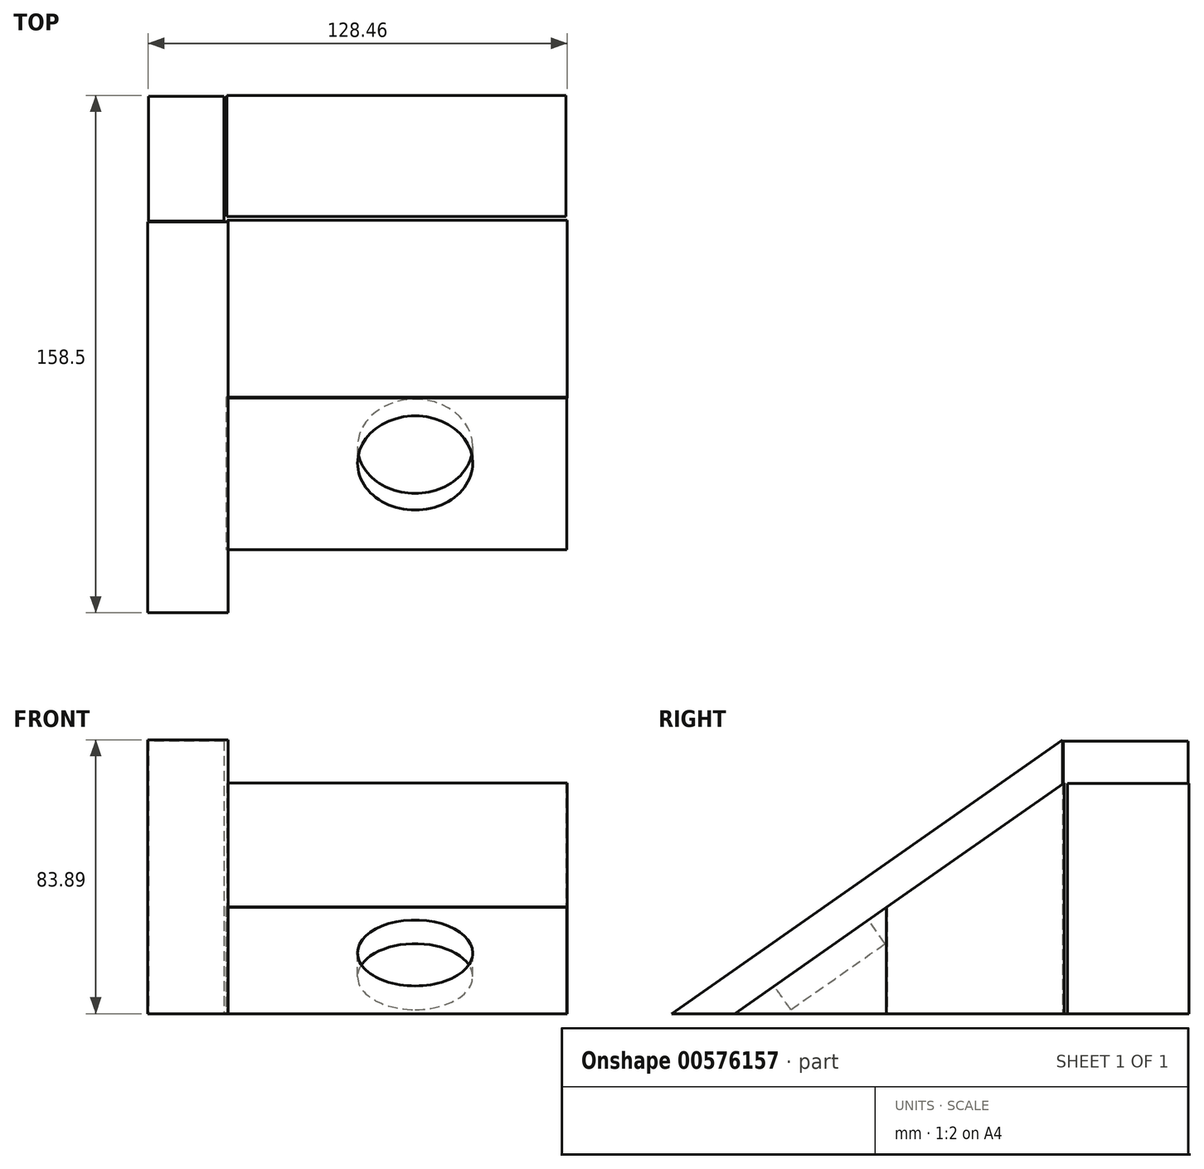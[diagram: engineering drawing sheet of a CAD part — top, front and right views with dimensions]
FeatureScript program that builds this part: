
annotation { "Feature Type Name" : "Feature", "Feature Type Description" : "" }
export const myFeature = defineFeature(function(context is Context, id is Id, definition is map)
    precondition{}
    {
        {
            var Q0;
            Q0=qCreatedBy(makeId("Top.planeOp"),FACE);
            var sketch = newSketch(context, id + "F0", { "sketchPlane" : qUnion([Q0])});
            skLineSegment(sketch, "E0.bottom", {"start": v(52.05, 27.2) * mm, "end": v(-52.05, 27.2) * mm});
            skLineSegment(sketch, "E0.top", {"start": v(52.05, -27.2) * mm, "end": v(-52.05, -27.2) * mm});
            skLineSegment(sketch, "E0.left", {"start": v(52.05, 27.2) * mm, "end": v(52.05, -27.2) * mm});
            skLineSegment(sketch, "E0.right", {"start": v(-52.05, 27.2) * mm, "end": v(-52.05, -27.2) * mm});
            skPoint(sketch, "E0.middle", {"position": v(0, 0) * mm});
            skSolve(sketch);
        }
        {
            var Q0;
            Q0=qCreatedBy(makeId("Top.planeOp"),FACE);
            var sketch = newSketch(context, id + "F1", { "sketchPlane" : qUnion([Q0])});
            skLineSegment(sketch, "E1.bottom", {"start": v(51.91, -27.03) * mm, "end": v(-52.53, -27.03) * mm});
            skLineSegment(sketch, "E1.top", {"start": v(51.91, -73.75) * mm, "end": v(-52.53, -73.75) * mm});
            skLineSegment(sketch, "E1.left", {"start": v(51.91, -27.03) * mm, "end": v(51.91, -73.75) * mm});
            skLineSegment(sketch, "E1.right", {"start": v(-52.53, -27.03) * mm, "end": v(-52.53, -73.75) * mm});
            skSolve(sketch);
        }
        {
            var Q0;
            Q0=sQuery(id+"F1.wireOp",EDGE,"E1.top");
            cPlane(context, id + "F2", {"entities" : qUnion([Q0]), "cplaneType" : CPlaneType.LINE_ANGLE, "offset" : 25.4 * mm, "angle" : 55 * degree, "width" : 152.4 * mm, "height" : 152.4 * mm});
        }
        {
            var Q0;
            Q0=makeQuery(id+"F0.imprint","IMPRINT",FACE,{"disambiguationData":[TD([[makeQuery(id+"F0.imprint","IMPRINT",EDGE,{"derivedFrom":sQuery(id+"F0.wireOp",EDGE,"E0.bottom")}),1.0]])]});
            var Q1;
            Q1=qCreatedBy(id+"F2.planeOp",FACE);
            extrude(context, id + "F3", {"entities" : qUnion([Q0]), "endBound" : BoundingType.UP_TO_SURFACE, "depth" : 25.4 * mm, "endBoundEntityFace" : qUnion([Q1]), "offsetDistance" : 25.4 * mm});
        }
        {
            var Q0;
            Q0=makeQuery(id+"F1.imprint","IMPRINT",FACE,{"disambiguationData":[TD([[makeQuery(id+"F1.imprint","IMPRINT",EDGE,{"derivedFrom":sQuery(id+"F1.wireOp",EDGE,"E1.bottom")}),1.0]])]});
            var Q1;
            Q1=qCreatedBy(id+"F2.planeOp",FACE);
            extrude(context, id + "F4", {"entities" : qUnion([Q0]), "endBound" : BoundingType.UP_TO_SURFACE, "depth" : 25.4 * mm, "endBoundEntityFace" : qUnion([Q1]), "offsetDistance" : 25.4 * mm});
        }
        {
            var Q0;
            Q0=makeQuery(id+"F4.opExtrude","CAP_FACE",FACE,{"disambiguationData":[OSD([sQuery(id+"F1.wireOp",EDGE,"E1.bottom"),sQuery(id+"F1.wireOp",EDGE,"E1.top"),sQuery(id+"F1.wireOp",EDGE,"E1.left"),sQuery(id+"F1.wireOp",EDGE,"E1.right")])],"isStart":false});
            var sketch = newSketch(context, id + "F5", { "sketchPlane" : qUnion([Q0])});
            skCircle(sketch, "E2", {"center": v(5.46, -27.96) * mm, "radius": 17.63 * mm});
            skSolve(sketch);
        }
        {
            var Q0;
            Q0=makeQuery(id+"F5.imprint","IMPRINT",FACE,{"disambiguationData":[TD([[makeQuery(id+"F5.imprint","IMPRINT",EDGE,{"derivedFrom":sQuery(id+"F5.wireOp",EDGE,"E2")}),1.0]])]});
            extrude(context, id + "F6", {"entities" : qUnion([Q0]), "operationType" : NewBodyOperationType.REMOVE, "oppositeDirection" : true, "depth" : 8.9 * mm, "offsetDistance" : 25.4 * mm});
        }
        {
            var Q0;
            Q0=qCreatedBy(makeId("Top.planeOp"),FACE);
            var sketch = newSketch(context, id + "F7", { "sketchPlane" : qUnion([Q0])});
            skLineSegment(sketch, "E3.bottom", {"start": v(-52.18, 28.3) * mm, "end": v(51.72, 28.3) * mm});
            skLineSegment(sketch, "E3.top", {"start": v(-52.18, 65.46) * mm, "end": v(51.72, 65.46) * mm});
            skLineSegment(sketch, "E3.left", {"start": v(-52.18, 28.3) * mm, "end": v(-52.18, 65.46) * mm});
            skLineSegment(sketch, "E3.right", {"start": v(51.72, 28.3) * mm, "end": v(51.72, 65.46) * mm});
            skSolve(sketch);
        }
        {
            var Q0;
            Q0=makeQuery(id+"F7.imprint","IMPRINT",FACE,{"disambiguationData":[TD([[makeQuery(id+"F7.imprint","IMPRINT",EDGE,{"derivedFrom":sQuery(id+"F7.wireOp",EDGE,"E3.bottom")}),1.0]])]});
            extrude(context, id + "F8", {"entities" : qUnion([Q0]), "depth" : 70.61 * mm, "offsetDistance" : 25.4 * mm});
        }
        {
            var Q0;
            Q0=qCreatedBy(makeId("Top.planeOp"),FACE);
            var sketch = newSketch(context, id + "F9", { "sketchPlane" : qUnion([Q0])});
            skLineSegment(sketch, "E4.bottom", {"start": v(-51.83, 26.77) * mm, "end": v(-76.41, 26.77) * mm});
            skLineSegment(sketch, "E4.top", {"start": v(-51.83, -93.04) * mm, "end": v(-76.41, -93.04) * mm});
            skLineSegment(sketch, "E4.left", {"start": v(-51.83, 26.77) * mm, "end": v(-51.83, -93.04) * mm});
            skLineSegment(sketch, "E4.right", {"start": v(-76.41, 26.77) * mm, "end": v(-76.41, -93.04) * mm});
            skSolve(sketch);
        }
        {
            var Q0;
            Q0=sQuery(id+"F9.wireOp",EDGE,"E4.top");
            cPlane(context, id + "F10", {"entities" : qUnion([Q0]), "cplaneType" : CPlaneType.LINE_ANGLE, "offset" : 25.4 * mm, "angle" : 55 * degree, "width" : 152.4 * mm, "height" : 152.4 * mm});
        }
        {
            var Q0;
            Q0=makeQuery(id+"F9.imprint","IMPRINT",FACE,{"disambiguationData":[TD([[makeQuery(id+"F9.imprint","IMPRINT",EDGE,{"derivedFrom":sQuery(id+"F9.wireOp",EDGE,"E4.bottom")}),1.0]])]});
            var Q1;
            Q1=qCreatedBy(id+"F10.planeOp",FACE);
            extrude(context, id + "F11", {"entities" : qUnion([Q0]), "endBound" : BoundingType.UP_TO_SURFACE, "depth" : 25.4 * mm, "endBoundEntityFace" : qUnion([Q1]), "offsetDistance" : 25.4 * mm});
        }
        {
            var Q0;
            Q0=qCreatedBy(makeId("Top.planeOp"),FACE);
            var sketch = newSketch(context, id + "F12", { "sketchPlane" : qUnion([Q0])});
            skLineSegment(sketch, "E5.bottom", {"start": v(-53.07, 65.24) * mm, "end": v(-76.2, 65.24) * mm});
            skLineSegment(sketch, "E5.top", {"start": v(-53.07, 26.95) * mm, "end": v(-76.2, 26.95) * mm});
            skLineSegment(sketch, "E5.left", {"start": v(-53.07, 65.24) * mm, "end": v(-53.07, 26.95) * mm});
            skLineSegment(sketch, "E5.right", {"start": v(-76.2, 65.24) * mm, "end": v(-76.2, 26.95) * mm});
            skSolve(sketch);
        }
        {
            var Q0;
            Q0=makeQuery(id+"F12.imprint","IMPRINT",FACE,{"disambiguationData":[TD([[makeQuery(id+"F12.imprint","IMPRINT",EDGE,{"derivedFrom":sQuery(id+"F12.wireOp",EDGE,"E5.bottom")}),1.0]])]});
            extrude(context, id + "F13", {"entities" : qUnion([Q0]), "depth" : 83.57 * mm, "offsetDistance" : 25.4 * mm});
        }
    });
